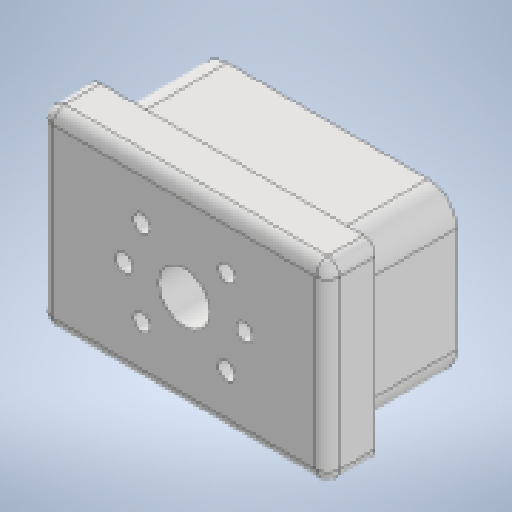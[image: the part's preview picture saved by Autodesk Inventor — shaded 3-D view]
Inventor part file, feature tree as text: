
AUTODESK INVENTOR PART (.ipt)
format: ipt  version: 2023 (Build 270158000, 158)  size: 208,896 bytes
history: native  units: in
note: dims shown in document units (in); Inventor stores cm internally (conversion verified against a paired STEP export)
features: extrude x3, sketch x3, projected_geometry x2, fillet x1, chamfer x1
ambient origin geometry x8: Origin, YZ Plane, XZ Plane, XY Plane, X Axis, Y Axis, Z Axis, Center Point
bodies: Solid1 (feature_tree)
feature tree (10):
  extrude  "Extrusion1"  Depth=1.7in
  extrude  "Extrusion2"  Depth=1.0in TaperAngle=0.0deg
  fillet  "Fillet1"  Radius=3.0in
  extrude  "Extrusion3"  Depth=0.125in
  chamfer  "Chamfer1"  Distance=0.5in
  sketch  "Sketch1"  dims[d0=2.7in d1=1.7in]
  sketch  "Sketch2"  dims[d2=0.3in d3=1.0in d4=0.0in d5=3.0in]
  sketch  "Sketch3"  dims[d6=2.0in d7=0.125in d8=0.5in d9=0.0in d10=0.125in d11=0.5315in d12=0.5in d13=0.0in d14=0.1772in d15=1.2598in d16=45.0deg d17=0.05in d18=0.125in d19=45.0deg]
  projected_geometry  "Projected Loop1"
  projected_geometry  "Projected Loop2"
